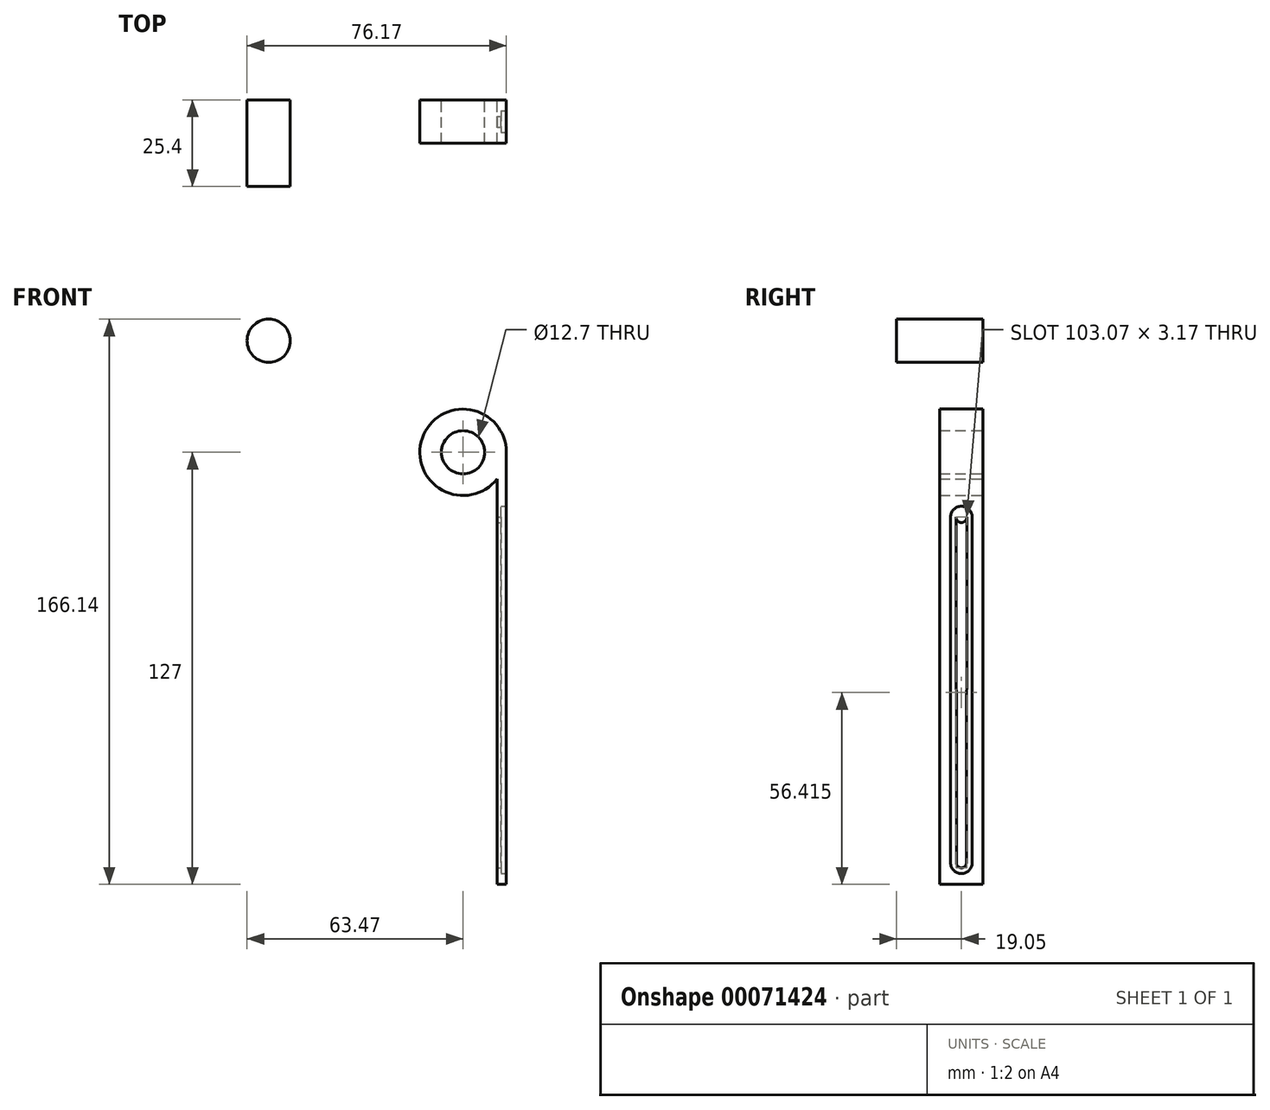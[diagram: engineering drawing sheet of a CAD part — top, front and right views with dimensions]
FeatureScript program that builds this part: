
annotation { "Feature Type Name" : "Feature", "Feature Type Description" : "" }
export const myFeature = defineFeature(function(context is Context, id is Id, definition is map)
    precondition{}
    {
        {
            var Q0;
            Q0=qCreatedBy(makeId("Front.planeOp"),FACE);
            var sketch = newSketch(context, id + "F0", { "sketchPlane" : qUnion([Q0])});
            skCircle(sketch, "E0", {"center": v(0, 0) * mm, "radius": 12.7 * mm});
            skLineSegment(sketch, "E1", {"start": v(12.7, 0) * mm, "end": v(12.7, -127) * mm});
            skLineSegment(sketch, "E2", {"start": v(12.7, -127) * mm, "end": v(9.98, -127) * mm});
            skLineSegment(sketch, "E3", {"start": v(9.98, -127) * mm, "end": v(9.98, -7.86) * mm});
            skCircle(sketch, "E4", {"center": v(0, 0) * mm, "radius": 6.35 * mm});
            skSolve(sketch);
        }
        {
            var Q0;
            Q0=makeQuery(id+"F0.imprint","IMPRINT",FACE,{"disambiguationData":[TD([[makeQuery(id+"F0.imprint","IMPRINT",EDGE,{"derivedFrom":sQuery(id+"F0.wireOp",EDGE,"E4")}),-1.0]])]});
            var Q1;
            {var subQ0=sQuery(id+"F0.wireOp",EDGE,"E1");Q1=makeQuery(id+"F0.imprint","IMPRINT",FACE,{"disambiguationData":[TD([[makeQuery(id+"F0.imprint","IMPRINT",EDGE,{"derivedFrom":subQ0}),-1.0]])]});}
            extrude(context, id + "F1", {"entities" : qUnion([Q0, Q1]), "depth" : 12.7 * mm});
        }
        {
            var Q0;
            Q0=qCreatedBy(makeId("Front.planeOp"),FACE);
            var sketch = newSketch(context, id + "F2", { "sketchPlane" : qUnion([Q0])});
            skCircle(sketch, "E5", {"center": v(-57.12, 32.79) * mm, "radius": 6.35 * mm});
            skSolve(sketch);
        }
        {
            var Q0;
            Q0 = qSketchRegion(id + "F2", true);
            extrude(context, id + "F3", {"entities" : qUnion([Q0]), "depth" : 25.4 * mm});
        }
        {
            var Q0;
            Q0=makeQuery(id+"F1.opExtrude","SWEPT_FACE",FACE,{"disambiguationData":[OSD([sQuery(id+"F0.wireOp",EDGE,"E1")])]});
            var sketch = newSketch(context, id + "F4", { "sketchPlane" : qUnion([Q0])});
            skLineSegment(sketch, "E6.0", {"start": v(0, 0) * mm, "end": v(0, -127) * mm});
            skLineSegment(sketch, "E6.1", {"start": v(-12.7, 0) * mm, "end": v(-12.7, -127) * mm});
            skLineSegment(sketch, "E6.2", {"start": v(-12.7, -127) * mm, "end": v(0, -127) * mm});
            skCircle(sketch, "E7", {"center": v(-6.35, -120.65) * mm, "radius": 3.18 * mm});
            skCircle(sketch, "E8", {"center": v(-6.35, -19.05) * mm, "radius": 3.18 * mm});
            skLineSegment(sketch, "E9", {"start": v(-3.17, -19.05) * mm, "end": v(-3.17, -120.65) * mm});
            skLineSegment(sketch, "E10", {"start": v(-9.52, -19.05) * mm, "end": v(-9.52, -120.65) * mm});
            skSolve(sketch);
        }
        {
            var Q0;
            {var subQ0=sQuery(id+"F4.wireOp",EDGE,"E8");var subQ1=makeQuery(id+"F4.imprint","INTERSECT",VERTEX,{"derivedFrom":[subQ0,sQuery(id+"F4.wireOp",EDGE,"E9")]});Q0=makeQuery(id+"F4.imprint","IMPRINT",FACE,{"disambiguationData":[TD([[makeQuery(id+"F4.imprint","IMPRINT",EDGE,{"disambiguationData":[TD([[subQ1,-1.0]])],"derivedFrom":subQ0}),1.0]])]});}
            var Q1;
            {var subQ0=sQuery(id+"F4.wireOp",EDGE,"E9");Q1=makeQuery(id+"F4.imprint","IMPRINT",FACE,{"disambiguationData":[TD([[makeQuery(id+"F4.imprint","IMPRINT",EDGE,{"derivedFrom":subQ0}),-1.0]])]});}
            var Q2;
            {var subQ0=sQuery(id+"F4.wireOp",EDGE,"E7");var subQ1=makeQuery(id+"F4.imprint","INTERSECT",VERTEX,{"derivedFrom":[subQ0,sQuery(id+"F4.wireOp",EDGE,"E9")]});Q2=makeQuery(id+"F4.imprint","IMPRINT",FACE,{"disambiguationData":[TD([[makeQuery(id+"F4.imprint","IMPRINT",EDGE,{"disambiguationData":[TD([[subQ1,-1.0]])],"derivedFrom":subQ0}),1.0]])]});}
            extrude(context, id + "F5", {"entities" : qUnion([Q0, Q1, Q2]), "operationType" : NewBodyOperationType.REMOVE, "oppositeDirection" : true, "depth" : 1.59 * mm});
        }
        {
            var Q0;
            Q0=makeQuery(id+"F5.boolean.opBoolean","COPY",FACE,{"derivedFrom":makeQuery(id+"F5.opExtrude","CAP_FACE",FACE,{"disambiguationData":[OSD([sQuery(id+"F4.wireOp",EDGE,"E7"),sQuery(id+"F4.wireOp",EDGE,"E8"),sQuery(id+"F4.wireOp",EDGE,"E9"),sQuery(id+"F4.wireOp",EDGE,"E10")])],"isStart":false})});
            var sketch = newSketch(context, id + "F6", { "sketchPlane" : qUnion([Q0])});
            skArc(sketch, "E11.0", {"start": v(-9.52, -120.65) * mm, "mid": v(-6.35, -123.83) * mm, "end": v(-3.17, -120.65) * mm});
            skLineSegment(sketch, "E11.1", {"start": v(-9.52, -19.05) * mm, "end": v(-9.52, -120.65) * mm});
            skLineSegment(sketch, "E11.2", {"start": v(-3.17, -19.05) * mm, "end": v(-3.17, -120.65) * mm});
            skArc(sketch, "E11.3", {"start": v(-3.17, -19.05) * mm, "mid": v(-6.35, -15.88) * mm, "end": v(-9.52, -19.05) * mm});
            skCircle(sketch, "E12", {"center": v(-6.35, -19.05) * mm, "radius": 1.59 * mm});
            skCircle(sketch, "E13", {"center": v(-6.35, -120.65) * mm, "radius": 1.47 * mm});
            skLineSegment(sketch, "E14", {"start": v(-7.82, -120.65) * mm, "end": v(-7.94, -19.05) * mm});
            skLineSegment(sketch, "E15", {"start": v(-4.76, -19.05) * mm, "end": v(-4.88, -120.65) * mm});
            skSolve(sketch);
        }
        {
            var Q0;
            {var subQ0=sQuery(id+"F6.wireOp",EDGE,"E12");var subQ2=makeQuery(id+"F6.imprint","IMPRINT",VERTEX,{"derivedFrom":subQ0});Q0=makeQuery(id+"F6.imprint","IMPRINT",FACE,{"disambiguationData":[TD([[makeQuery(id+"F6.imprint","IMPRINT",EDGE,{"disambiguationData":[TD([[subQ2,-1.0]])],"derivedFrom":subQ0}),1.0]])]});}
            var Q1;
            {var subQ0=sQuery(id+"F6.wireOp",EDGE,"E14");Q1=makeQuery(id+"F6.imprint","IMPRINT",FACE,{"disambiguationData":[TD([[makeQuery(id+"F6.imprint","IMPRINT",EDGE,{"derivedFrom":subQ0}),-1.0]])]});}
            var Q2;
            {var subQ0=sQuery(id+"F6.wireOp",EDGE,"E13");var subQ1=makeQuery(id+"F6.imprint","INTERSECT",VERTEX,{"derivedFrom":[subQ0,sQuery(id+"F6.wireOp",EDGE,"E14")]});Q2=makeQuery(id+"F6.imprint","IMPRINT",FACE,{"disambiguationData":[TD([[makeQuery(id+"F6.imprint","IMPRINT",EDGE,{"disambiguationData":[TD([[subQ1,-1.0]])],"derivedFrom":subQ0}),1.0]])]});}
            extrude(context, id + "F7", {"entities" : qUnion([Q0, Q1, Q2]), "operationType" : NewBodyOperationType.REMOVE, "endBound" : BoundingType.THROUGH_ALL, "oppositeDirection" : true, "depth" : 25.4 * mm});
        }
    });
